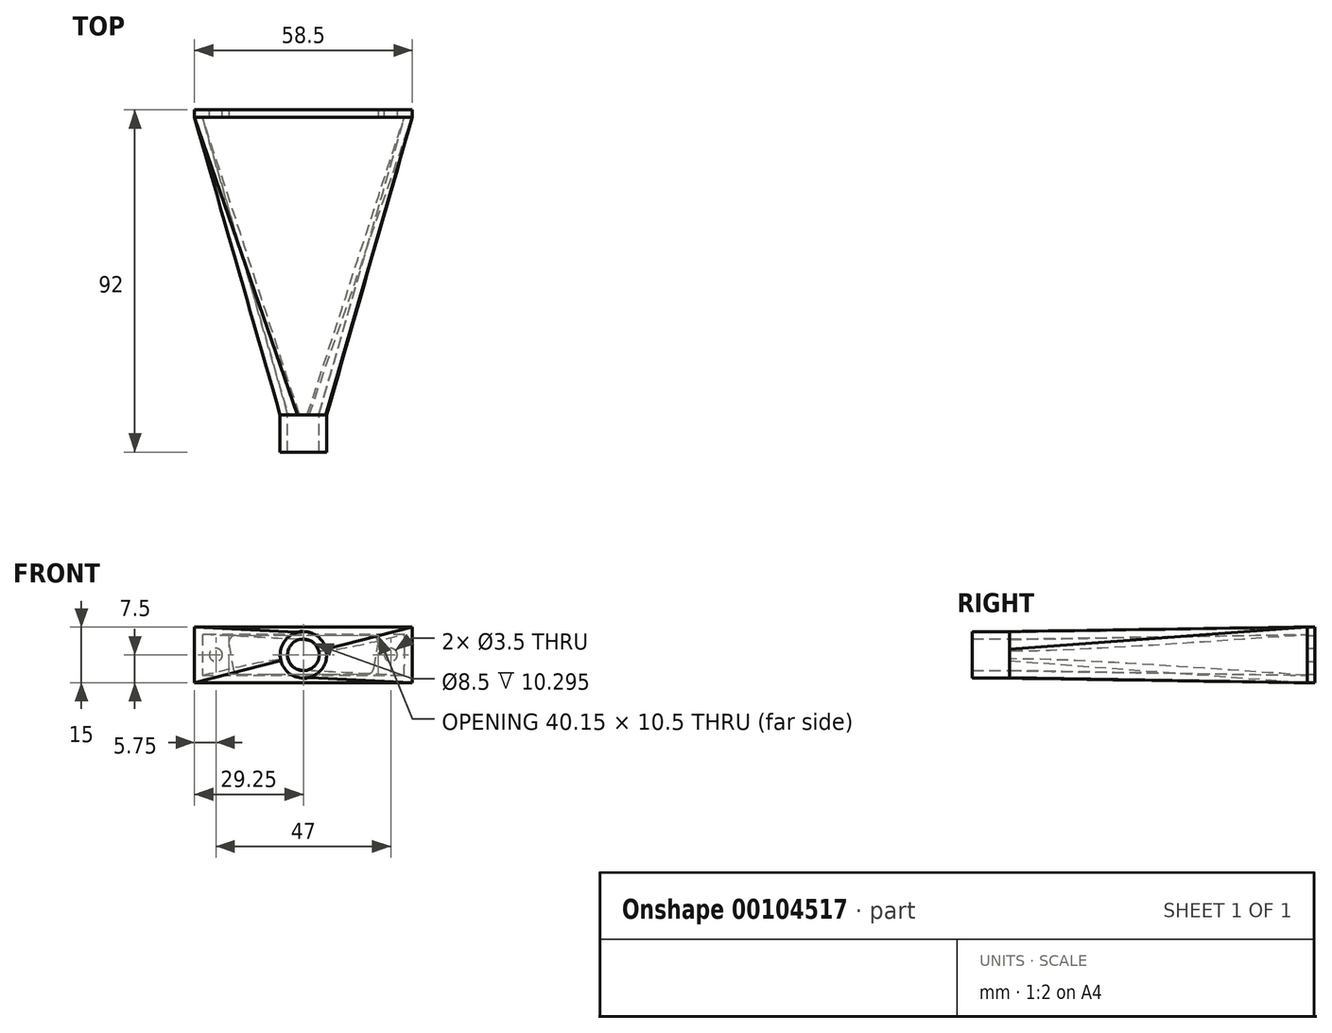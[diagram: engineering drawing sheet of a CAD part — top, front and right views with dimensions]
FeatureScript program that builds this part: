
annotation { "Feature Type Name" : "Feature", "Feature Type Description" : "" }
export const myFeature = defineFeature(function(context is Context, id is Id, definition is map)
    precondition{}
    {
        {
            var Q0;
            Q0=qCreatedBy(makeId("Front.planeOp"),FACE);
            var sketch = newSketch(context, id + "F0", { "sketchPlane" : qUnion([Q0])});
            skLineSegment(sketch, "E0.bottom", {"start": v(-29.25, -7.5) * mm, "end": v(29.25, -7.5) * mm});
            skLineSegment(sketch, "E0.top", {"start": v(-29.25, 7.5) * mm, "end": v(29.25, 7.5) * mm});
            skLineSegment(sketch, "E0.left", {"start": v(-29.25, -7.5) * mm, "end": v(-29.25, 7.5) * mm});
            skLineSegment(sketch, "E0.right", {"start": v(29.25, -7.5) * mm, "end": v(29.25, 7.5) * mm});
            skPoint(sketch, "E0.middle", {"position": v(0, 0) * mm});
            skPoint(sketch, "E0.middle.positionSnap0", {"position": v(-165.7, -8.86) * mm});
            skPoint(sketch, "E0.centerSnap0", {"position": v(-165.7, -8.86) * mm});
            skCircle(sketch, "E1", {"center": v(-23.5, 0) * mm, "radius": 1.75 * mm});
            skCircle(sketch, "E2", {"center": v(23.5, 0) * mm, "radius": 1.75 * mm});
            skLineSegment(sketch, "E3", {"start": v(-18.6, -5.25) * mm, "end": v(18.6, -5.25) * mm});
            skLineSegment(sketch, "E4", {"start": v(18.6, -5.25) * mm, "end": v(20.46, 5.25) * mm});
            skLineSegment(sketch, "E5", {"start": v(20.46, 5.25) * mm, "end": v(-20.46, 5.25) * mm});
            skLineSegment(sketch, "E6", {"start": v(-20.46, 5.25) * mm, "end": v(-18.6, -5.25) * mm});
            skSolve(sketch);
        }
        {
            var Q0;
            Q0=makeQuery(id+"F0.imprint","IMPRINT",FACE,{"disambiguationData":[TD([[makeQuery(id+"F0.imprint","IMPRINT",EDGE,{"derivedFrom":sQuery(id+"F0.wireOp",EDGE,"E0.bottom")}),1.0]])]});
            var Q1;
            Q1=makeQuery(id+"F0.imprint","IMPRINT",FACE,{"disambiguationData":[TD([[makeQuery(id+"F0.imprint","IMPRINT",EDGE,{"derivedFrom":sQuery(id+"F0.wireOp",EDGE,"E3")}),1.0]])]});
            var Q2;
            Q2=makeQuery(id+"F0.imprint","IMPRINT",FACE,{"disambiguationData":[TD([[makeQuery(id+"F0.imprint","IMPRINT",EDGE,{"derivedFrom":sQuery(id+"F0.wireOp",EDGE,"E2")}),1.0]])]});
            var Q3;
            Q3=makeQuery(id+"F0.imprint","IMPRINT",FACE,{"disambiguationData":[TD([[makeQuery(id+"F0.imprint","IMPRINT",EDGE,{"derivedFrom":sQuery(id+"F0.wireOp",EDGE,"E1")}),1.0]])]});
            extrude(context, id + "F1", {"entities" : qUnion([Q0, Q1, Q2, Q3]), "depth" : 2 * mm});
        }
        {
            var Q0;
            Q0=makeQuery(id+"F1.opExtrude","CAP_FACE",FACE,{"disambiguationData":[OSD([sQuery(id+"F0.wireOp",EDGE,"E0.bottom"),sQuery(id+"F0.wireOp",EDGE,"E0.top"),sQuery(id+"F0.wireOp",EDGE,"E0.left"),sQuery(id+"F0.wireOp",EDGE,"E0.right"),sQuery(id+"F0.wireOp",EDGE,"E1"),sQuery(id+"F0.wireOp",EDGE,"E2"),sQuery(id+"F0.wireOp",EDGE,"E3"),sQuery(id+"F0.wireOp",EDGE,"E4"),sQuery(id+"F0.wireOp",EDGE,"E5"),sQuery(id+"F0.wireOp",EDGE,"E6")])],"isStart":false});
            cPlane(context, id + "F2", {"entities" : qUnion([Q0]), "cplaneType" : CPlaneType.OFFSET, "offset" : 80 * mm, "width" : 150 * mm, "height" : 150 * mm});
        }
        {
            var Q0;
            Q0=qCreatedBy(id+"F2.planeOp",FACE);
            var sketch = newSketch(context, id + "F3", { "sketchPlane" : qUnion([Q0])});
            skCircle(sketch, "E7", {"center": v(0, 0) * mm, "radius": 4.25 * mm});
            skCircle(sketch, "E8", {"center": v(0, 0) * mm, "radius": 6.25 * mm});
            skSolve(sketch);
        }
        {
            var Q0;
            Q0=makeQuery(id+"F3.imprint","IMPRINT",FACE,{"disambiguationData":[TD([[makeQuery(id+"F3.imprint","IMPRINT",EDGE,{"derivedFrom":sQuery(id+"F3.wireOp",EDGE,"E7")}),-1.0]])]});
            var Q1;
            Q1=makeQuery(id+"F3.imprint","IMPRINT",FACE,{"disambiguationData":[TD([[makeQuery(id+"F3.imprint","IMPRINT",EDGE,{"derivedFrom":sQuery(id+"F3.wireOp",EDGE,"E7")}),1.0]])]});
            extrude(context, id + "F4", {"entities" : qUnion([Q0, Q1]), "depth" : 10 * mm});
        }
        {
            var Q0;
            Q0=makeQuery(id+"F4.opExtrude","CAP_FACE",FACE,{"disambiguationData":[OSD([sQuery(id+"F3.wireOp",EDGE,"E8")])],"isStart":true});
            var Q1;
            Q1=makeQuery(id+"F1.opExtrude","CAP_FACE",FACE,{"disambiguationData":[OSD([sQuery(id+"F0.wireOp",EDGE,"E0.bottom"),sQuery(id+"F0.wireOp",EDGE,"E0.top"),sQuery(id+"F0.wireOp",EDGE,"E0.left"),sQuery(id+"F0.wireOp",EDGE,"E0.right")])],"isStart":false});
            loft(context, id + "F5", {"operationType" : NewBodyOperationType.ADD, "sheetProfilesArray" : [{ "sheetProfileEntities" : qUnion([Q0]) }, { "sheetProfileEntities" : qUnion([Q1]) }]});
        }
        {
            var Q0;
            Q0=makeQuery(id+"F4.opExtrude","CAP_FACE",FACE,{"disambiguationData":[OSD([sQuery(id+"F3.wireOp",EDGE,"E8")])],"isStart":false});
            shell(context, id + "F6", {"entities" : qUnion([Q0]), "thickness" : 2 * mm});
        }
        {
            var Q0;
            Q0=makeQuery(id+"F0.imprint","IMPRINT",FACE,{"disambiguationData":[TD([[makeQuery(id+"F0.imprint","IMPRINT",EDGE,{"derivedFrom":sQuery(id+"F0.wireOp",EDGE,"E3")}),1.0]])]});
            var Q1;
            Q1=makeQuery(id+"F0.imprint","IMPRINT",FACE,{"disambiguationData":[TD([[makeQuery(id+"F0.imprint","IMPRINT",EDGE,{"derivedFrom":sQuery(id+"F0.wireOp",EDGE,"E2")}),1.0]])]});
            var Q2;
            Q2=makeQuery(id+"F0.imprint","IMPRINT",FACE,{"disambiguationData":[TD([[makeQuery(id+"F0.imprint","IMPRINT",EDGE,{"derivedFrom":sQuery(id+"F0.wireOp",EDGE,"E1")}),1.0]])]});
            extrude(context, id + "F7", {"entities" : qUnion([Q0, Q1, Q2]), "operationType" : NewBodyOperationType.REMOVE, "depth" : 2 * mm});
        }
        {
            var Q0;
            Q0=makeQuery(id+"F7.boolean.opBoolean","COPY",EDGE,{"derivedFrom":makeQuery(id+"F7.opExtrude","SWEPT_EDGE",EDGE,{"disambiguationData":[OSD([sQuery(id+"F0.wireOp",EDGE,"E4"),sQuery(id+"F0.wireOp",EDGE,"E5")])]})});
            var Q1;
            Q1=makeQuery(id+"F7.boolean.opBoolean","COPY",EDGE,{"derivedFrom":makeQuery(id+"F7.opExtrude","SWEPT_EDGE",EDGE,{"disambiguationData":[OSD([sQuery(id+"F0.wireOp",EDGE,"E3"),sQuery(id+"F0.wireOp",EDGE,"E4")])]})});
            var Q2;
            Q2=makeQuery(id+"F7.boolean.opBoolean","COPY",EDGE,{"derivedFrom":makeQuery(id+"F7.opExtrude","SWEPT_EDGE",EDGE,{"disambiguationData":[OSD([sQuery(id+"F0.wireOp",EDGE,"E5"),sQuery(id+"F0.wireOp",EDGE,"E6")])]})});
            var Q3;
            Q3=makeQuery(id+"F7.boolean.opBoolean","COPY",EDGE,{"derivedFrom":makeQuery(id+"F7.opExtrude","SWEPT_EDGE",EDGE,{"disambiguationData":[OSD([sQuery(id+"F0.wireOp",EDGE,"E3"),sQuery(id+"F0.wireOp",EDGE,"E6")])]})});
            fillet(context, id + "F8", {"entities" : qUnion([Q0, Q1, Q2, Q3]), "radius" : 2 * mm, "tangentPropagation" : true, "allowEdgeOverflow" : false});
        }
    });
